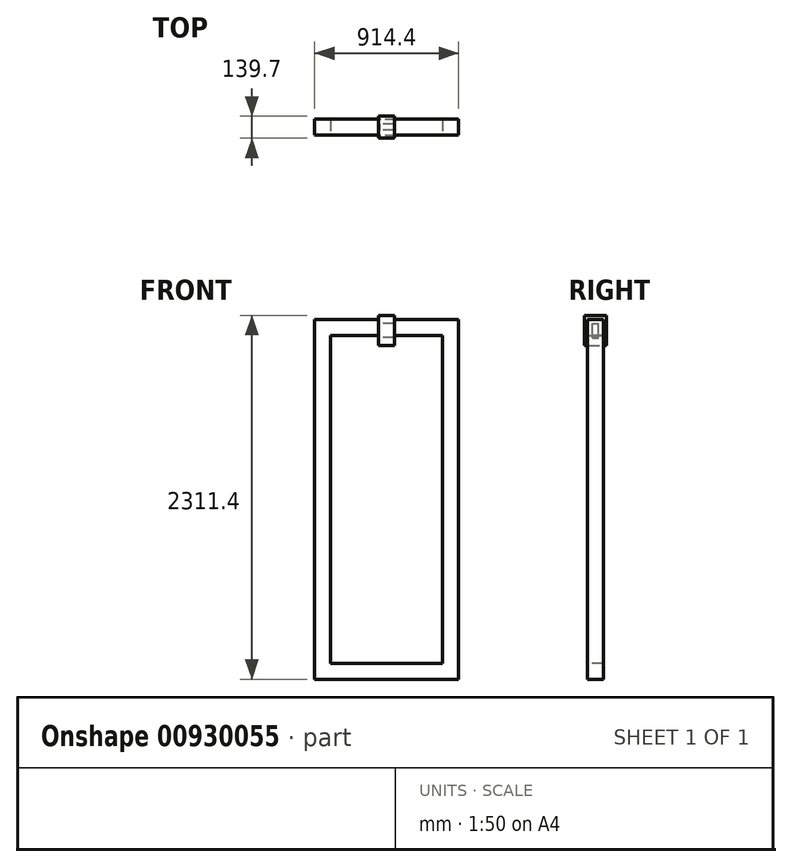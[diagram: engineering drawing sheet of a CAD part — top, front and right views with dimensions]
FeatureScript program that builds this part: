
annotation { "Feature Type Name" : "Feature", "Feature Type Description" : "" }
export const myFeature = defineFeature(function(context is Context, id is Id, definition is map)
    precondition{}
    {
        {
            var Q0;
            Q0=qCreatedBy(makeId("Top.planeOp"),FACE);
            var sketch = newSketch(context, id + "F0", { "sketchPlane" : qUnion([Q0])});
            skLineSegment(sketch, "E0.bottom", {"start": v(-457.2, 50.8) * mm, "end": v(457.2, 50.8) * mm});
            skLineSegment(sketch, "E0.top", {"start": v(-457.2, -50.8) * mm, "end": v(457.2, -50.8) * mm});
            skLineSegment(sketch, "E0.left", {"start": v(-457.2, 50.8) * mm, "end": v(-457.2, -50.8) * mm});
            skLineSegment(sketch, "E0.right", {"start": v(457.2, 50.8) * mm, "end": v(457.2, -50.8) * mm});
            skPoint(sketch, "E0.middle", {"position": v(0, 0) * mm});
            skSolve(sketch);
        }
        {
            var Q0;
            Q0 = qSketchRegion(id + "F0", true);
            extrude(context, id + "F1", {"entities" : qUnion([Q0]), "depth" : 2286 * mm, "offsetDistance" : 25.4 * mm});
        }
        {
            var Q0;
            Q0=makeQuery(id+"F1.opExtrude","SWEPT_FACE",FACE,{"disambiguationData":[OSD([sQuery(id+"F0.wireOp",EDGE,"E0.top")])]});
            var Q1;
            Q1=makeQuery(id+"F1.opExtrude","SWEPT_FACE",FACE,{"disambiguationData":[OSD([sQuery(id+"F0.wireOp",EDGE,"E0.bottom")])]});
            shell(context, id + "F2", {"entities" : qUnion([Q0, Q1]), "thickness" : 101.6 * mm});
        }
        {
            var Q0;
            Q0=makeQuery(id+"F1.opExtrude","CAP_FACE",FACE,{"disambiguationData":[OSD([sQuery(id+"F0.wireOp",EDGE,"E0.bottom"),sQuery(id+"F0.wireOp",EDGE,"E0.top"),sQuery(id+"F0.wireOp",EDGE,"E0.left"),sQuery(id+"F0.wireOp",EDGE,"E0.right")])],"isStart":false});
            var sketch = newSketch(context, id + "F3", { "sketchPlane" : qUnion([Q0])});
            skLineSegment(sketch, "E1.bottom", {"start": v(50.8, -69.85) * mm, "end": v(-50.8, -69.85) * mm});
            skLineSegment(sketch, "E1.top", {"start": v(50.8, 69.85) * mm, "end": v(-50.8, 69.85) * mm});
            skLineSegment(sketch, "E1.left", {"start": v(50.8, -69.85) * mm, "end": v(50.8, 69.85) * mm});
            skLineSegment(sketch, "E1.right", {"start": v(-50.8, -69.85) * mm, "end": v(-50.8, 69.85) * mm});
            skPoint(sketch, "E1.middle", {"position": v(0, 0) * mm});
            skSolve(sketch);
        }
        {
            var Q0;
            Q0 = qSketchRegion(id + "F3", true);
            extrude(context, id + "F4", {"entities" : qUnion([Q0]), "operationType" : NewBodyOperationType.ADD, "oppositeDirection" : true, "depth" : 165.1 * mm, "offsetDistance" : 25.4 * mm, "hasSecondDirection" : true, "secondDirectionOppositeDirection" : false, "secondDirectionDepth" : 25.4 * mm});
        }
        {
            var Q0;
            Q0=makeQuery(id+"F4.opExtrude","SWEPT_FACE",FACE,{"disambiguationData":[OSD([sQuery(id+"F3.wireOp",EDGE,"E1.right")])]});
            var Q1;
            Q1=makeQuery(id+"F4.opExtrude","SWEPT_FACE",FACE,{"disambiguationData":[OSD([sQuery(id+"F3.wireOp",EDGE,"E1.left")])]});
            shell(context, id + "F5", {"entities" : qUnion([Q0, Q1]), "thickness" : 50.8 * mm});
        }
        {
            var Q0;
            {var subQ0=sQuery(id+"F3.wireOp",EDGE,"E1.right");Q0=makeQuery(id+"F5.opShell","OFFSET_EDGE",EDGE,{"disambiguationData":[OSD([subQ0]),TDD([makeQuery(id+"F4.opExtrude","CAP_EDGE",EDGE,{"disambiguationData":[OSD([subQ0])],"isStart":false})])]});}
            chamfer(context, id + "F6", {"entities" : qUnion([Q0]), "width" : 5.08 * mm, "tangentPropagation" : true});
        }
    });
